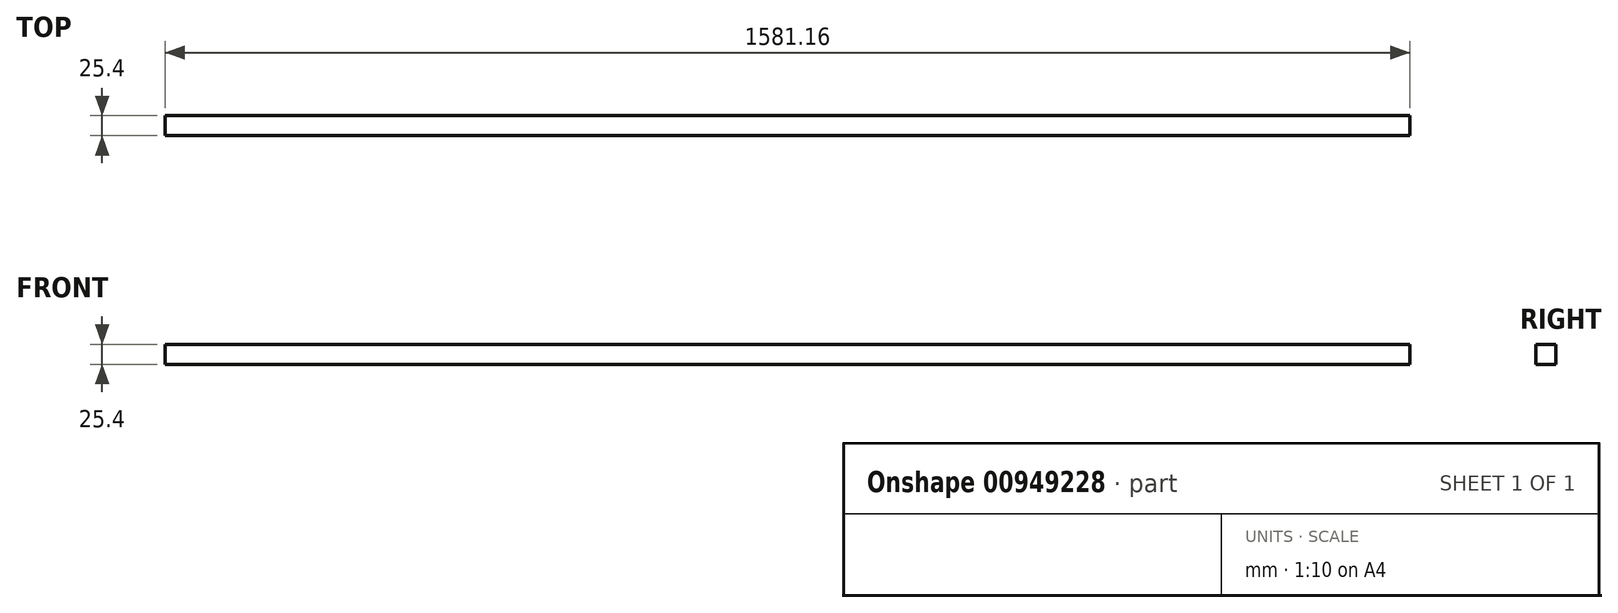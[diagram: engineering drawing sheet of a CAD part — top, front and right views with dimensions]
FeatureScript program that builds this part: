
annotation { "Feature Type Name" : "Feature", "Feature Type Description" : "" }
export const myFeature = defineFeature(function(context is Context, id is Id, definition is map)
    precondition{}
    {
        {
            var Q0;
            Q0=qCreatedBy(makeId("Right.planeOp"),FACE);
            var sketch = newSketch(context, id + "F0", { "sketchPlane" : qUnion([Q0])});
            skLineSegment(sketch, "E0.bottom", {"start": v(-12.7, 12.7) * mm, "end": v(12.7, 12.7) * mm});
            skLineSegment(sketch, "E0.top", {"start": v(-12.7, -12.7) * mm, "end": v(12.7, -12.7) * mm});
            skLineSegment(sketch, "E0.left", {"start": v(-12.7, 12.7) * mm, "end": v(-12.7, -12.7) * mm});
            skLineSegment(sketch, "E0.right", {"start": v(12.7, 12.7) * mm, "end": v(12.7, -12.7) * mm});
            skPoint(sketch, "E0.middle", {"position": v(0, 0) * mm});
            skSolve(sketch);
        }
        {
            var Q0;
            Q0 = qSketchRegion(id + "F0", true);
            extrude(context, id + "F1", {"entities" : qUnion([Q0]), "endBound" : BoundingType.SYMMETRIC, "depth" : (62.25 * 25.4) * mm, "offsetDistance" : 25 * mm});
        }
    });
